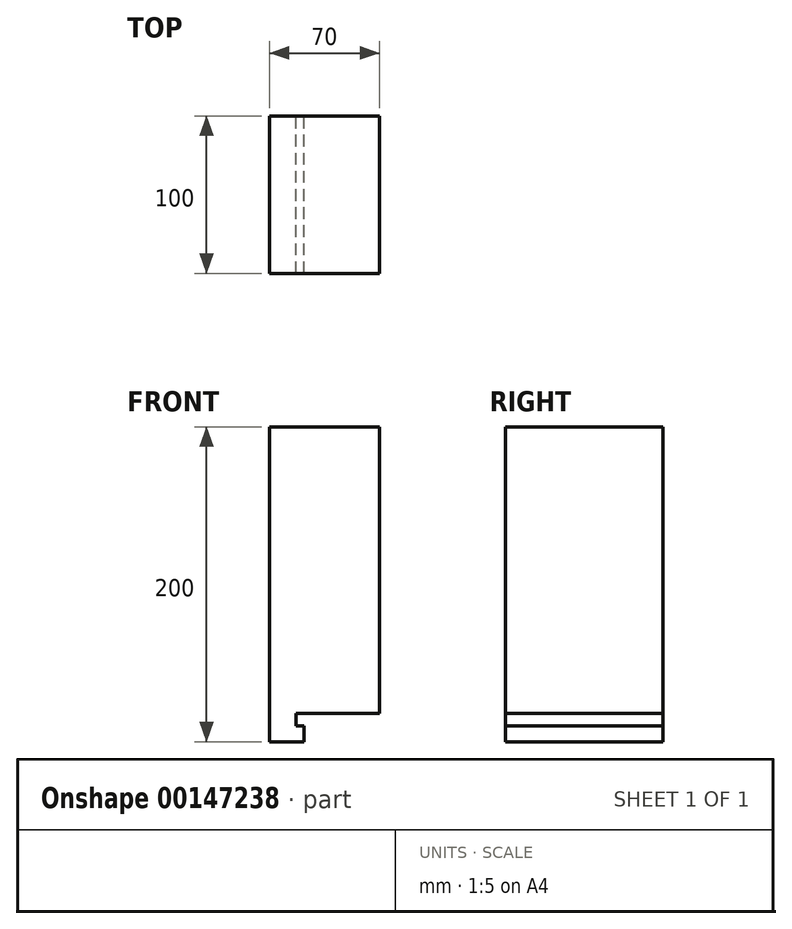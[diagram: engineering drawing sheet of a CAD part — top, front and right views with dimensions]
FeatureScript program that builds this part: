
annotation { "Feature Type Name" : "Feature", "Feature Type Description" : "" }
export const myFeature = defineFeature(function(context is Context, id is Id, definition is map)
    precondition{}
    {
        {
            var Q0;
            Q0=qCreatedBy(makeId("Front.planeOp"),FACE);
            var sketch = newSketch(context, id + "F0", { "sketchPlane" : qUnion([Q0])});
            skLineSegment(sketch, "E0", {"start": v(0, 200) * mm, "end": v(0, 0) * mm});
            skLineSegment(sketch, "E1", {"start": v(0, 0) * mm, "end": v(22, 0) * mm});
            skLineSegment(sketch, "E2", {"start": v(22, 0) * mm, "end": v(22, 10) * mm});
            skLineSegment(sketch, "E3", {"start": v(17, 18) * mm, "end": v(70, 18) * mm});
            skLineSegment(sketch, "E4", {"start": v(70, 18) * mm, "end": v(70, 200) * mm});
            skLineSegment(sketch, "E5", {"start": v(70, 200) * mm, "end": v(0, 200) * mm});
            skLineSegment(sketch, "E6", {"start": v(22, 10) * mm, "end": v(17, 10) * mm});
            skLineSegment(sketch, "E7", {"start": v(17, 10) * mm, "end": v(17, 18) * mm});
            skSolve(sketch);
        }
        {
            var Q0;
            Q0 = qSketchRegion(id + "F0", true);
            extrude(context, id + "F1", {"entities" : qUnion([Q0]), "depth" : 100 * mm});
        }
    });
